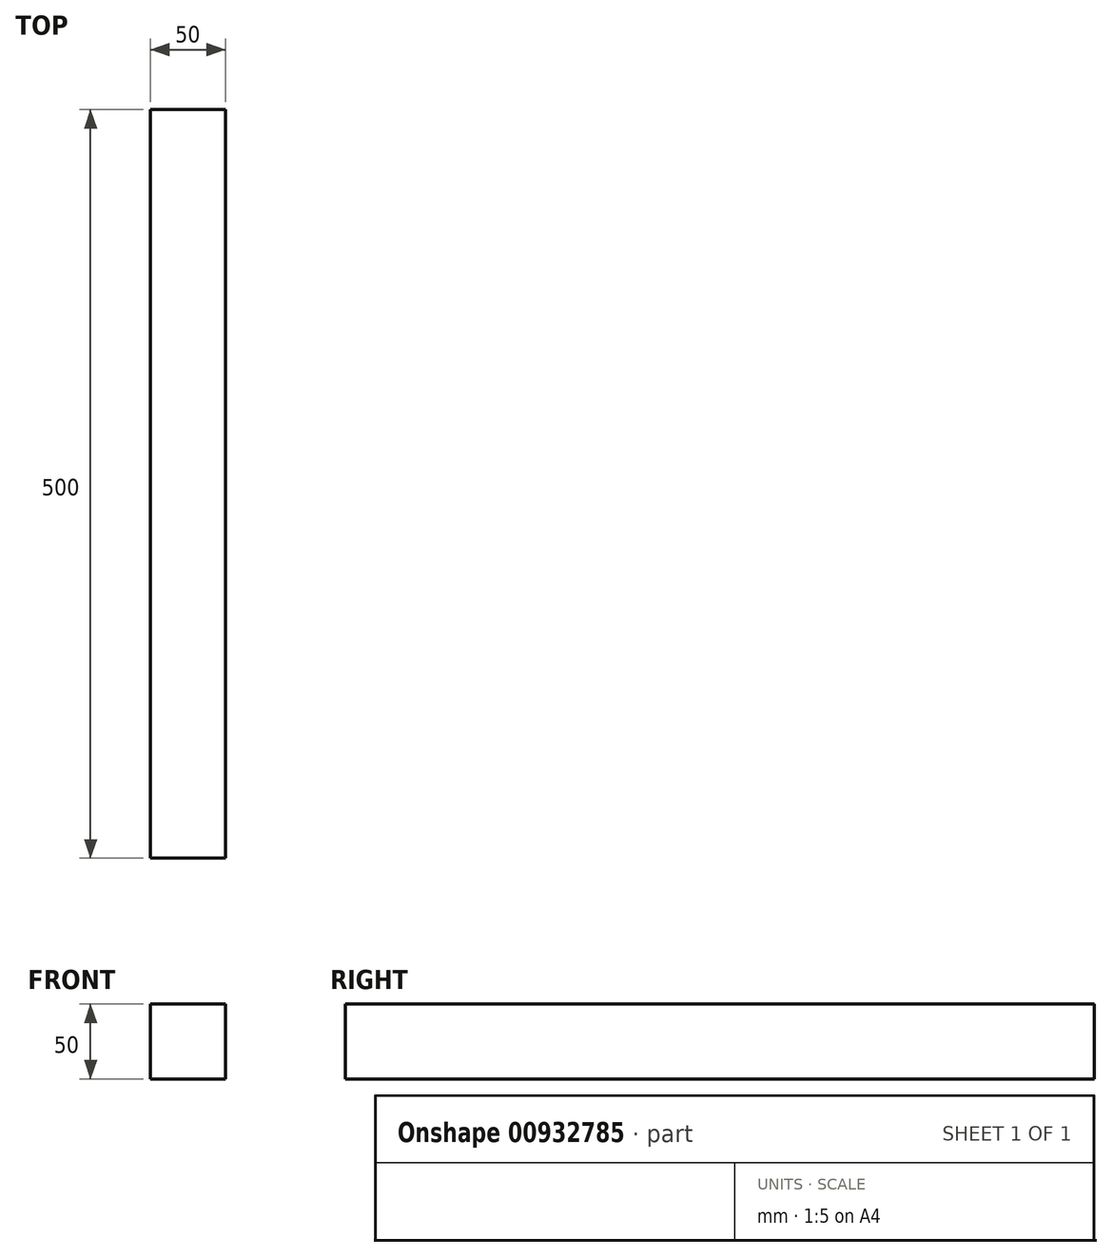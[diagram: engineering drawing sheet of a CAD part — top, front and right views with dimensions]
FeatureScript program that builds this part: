
annotation { "Feature Type Name" : "Feature", "Feature Type Description" : "" }
export const myFeature = defineFeature(function(context is Context, id is Id, definition is map)
    precondition{}
    {
        {
            var Q0;
            Q0=qCreatedBy(makeId("Front.planeOp"),FACE);
            var sketch = newSketch(context, id + "F0", { "sketchPlane" : qUnion([Q0])});
            skLineSegment(sketch, "E0.bottom", {"start": v(-85.44, 39.4) * mm, "end": v(-35.44, 39.4) * mm});
            skLineSegment(sketch, "E0.top", {"start": v(-85.44, -10.6) * mm, "end": v(-35.44, -10.6) * mm});
            skLineSegment(sketch, "E0.left", {"start": v(-85.44, 39.4) * mm, "end": v(-85.44, -10.6) * mm});
            skLineSegment(sketch, "E0.right", {"start": v(-35.44, 39.4) * mm, "end": v(-35.44, -10.6) * mm});
            skSolve(sketch);
        }
        {
            var Q0;
            Q0 = qSketchRegion(id + "F0", true);
            extrude(context, id + "F1", {"entities" : qUnion([Q0]), "depth" : 500 * mm, "offsetDistance" : 25 * mm});
        }
    });
